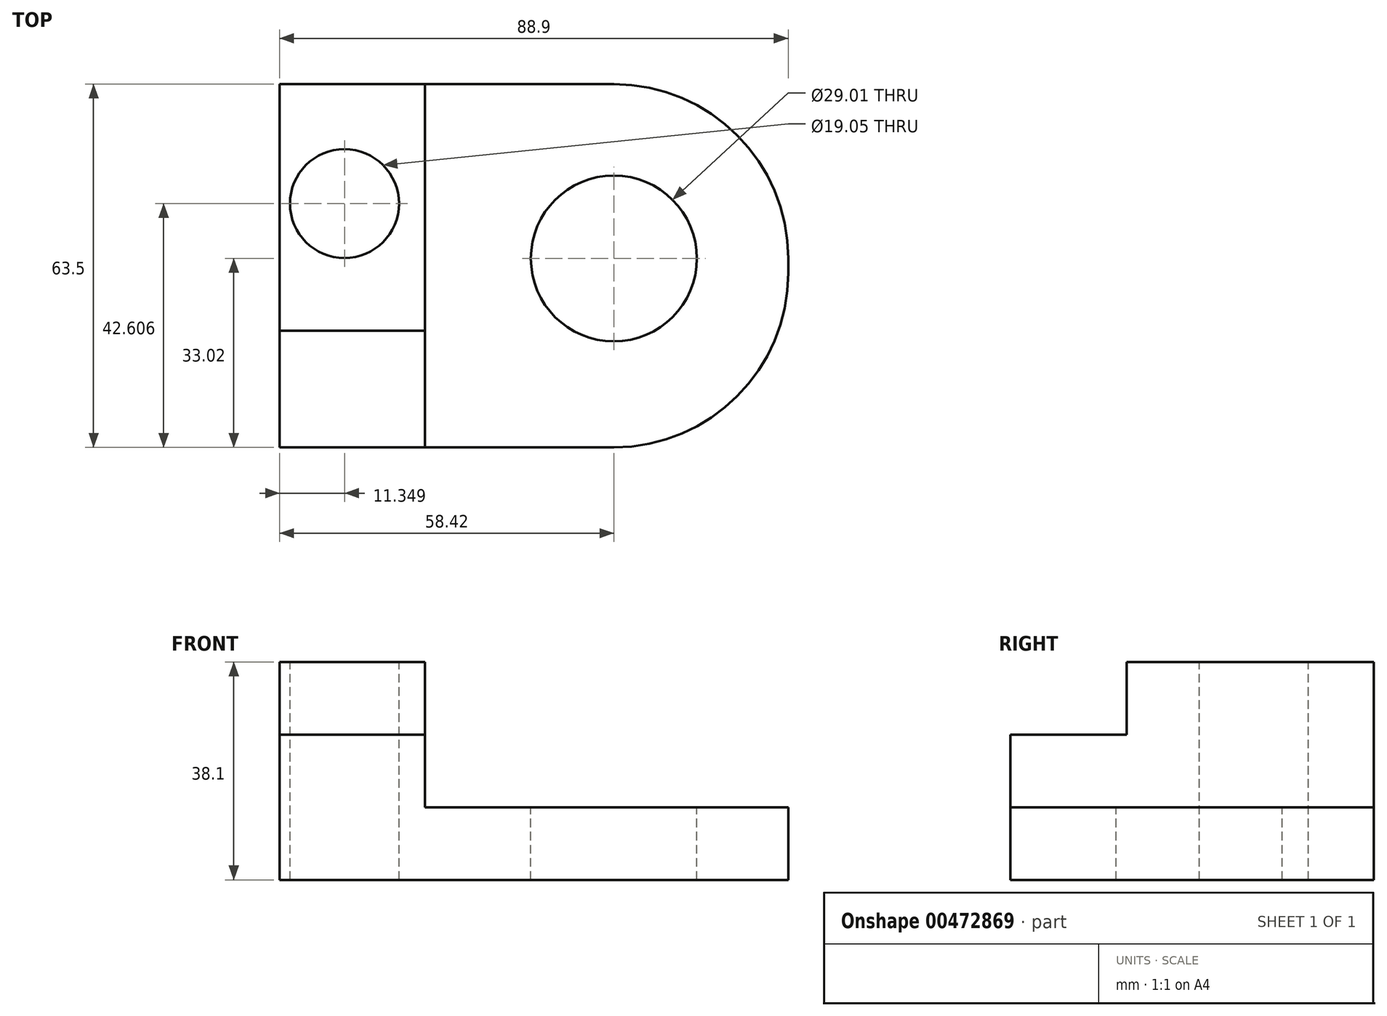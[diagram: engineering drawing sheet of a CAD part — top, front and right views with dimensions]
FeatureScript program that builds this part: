
annotation { "Feature Type Name" : "Feature", "Feature Type Description" : "" }
export const myFeature = defineFeature(function(context is Context, id is Id, definition is map)
    precondition{}
    {
        {
            var Q0;
            Q0=qCreatedBy(makeId("Top.planeOp"),FACE);
            var sketch = newSketch(context, id + "F0", { "sketchPlane" : qUnion([Q0])});
            skLineSegment(sketch, "E0.bottom", {"start": v(13.97, 31.75) * mm, "end": v(-44.45, 31.75) * mm});
            skLineSegment(sketch, "E0.top", {"start": v(13.97, -31.75) * mm, "end": v(-44.45, -31.75) * mm});
            skLineSegment(sketch, "E0.left", {"start": v(44.45, 1.27) * mm, "end": v(44.45, -1.27) * mm});
            skLineSegment(sketch, "E0.right", {"start": v(-44.45, 31.75) * mm, "end": v(-44.45, -31.75) * mm});
            skPoint(sketch, "E0.middle", {"position": v(0, 0) * mm});
            skPoint(sketch, "E1.visualSharp", {"position": v(44.45, 31.75) * mm});
            skArc(sketch, "E1.filletArc", {"start": v(44.45, 1.27) * mm, "mid": v(35.52, 22.82) * mm, "end": v(13.97, 31.75) * mm});
            skPoint(sketch, "E2.visualSharp", {"position": v(44.45, -31.75) * mm});
            skArc(sketch, "E2.filletArc", {"start": v(13.97, -31.75) * mm, "mid": v(35.52, -22.82) * mm, "end": v(44.45, -1.27) * mm});
            skSolve(sketch);
        }
        {
            var Q0;
            Q0=makeQuery(id+"F0.imprint","IMPRINT",FACE,{"disambiguationData":[TD([[makeQuery(id+"F0.imprint","IMPRINT",EDGE,{"derivedFrom":sQuery(id+"F0.wireOp",EDGE,"E0.bottom")}),1.0]])]});
            extrude(context, id + "F1", {"entities" : qUnion([Q0]), "depth" : 12.7 * mm});
        }
        {
            var Q0;
            Q0=makeQuery(id+"F1.opExtrude","CAP_FACE",FACE,{"disambiguationData":[OSD([sQuery(id+"F0.wireOp",EDGE,"E0.bottom"),sQuery(id+"F0.wireOp",EDGE,"E0.top"),sQuery(id+"F0.wireOp",EDGE,"E0.left"),sQuery(id+"F0.wireOp",EDGE,"E0.right"),sQuery(id+"F0.wireOp",EDGE,"E1.filletArc"),sQuery(id+"F0.wireOp",EDGE,"E2.filletArc")])],"isStart":false});
            var sketch = newSketch(context, id + "F2", { "sketchPlane" : qUnion([Q0])});
            skLineSegment(sketch, "E3.bottom", {"start": v(-44.45, -31.75) * mm, "end": v(-19.05, -31.75) * mm});
            skLineSegment(sketch, "E3.top", {"start": v(-44.45, 31.75) * mm, "end": v(-19.05, 31.75) * mm});
            skLineSegment(sketch, "E3.left", {"start": v(-44.45, -31.75) * mm, "end": v(-44.45, 31.75) * mm});
            skLineSegment(sketch, "E3.right", {"start": v(-19.05, -31.75) * mm, "end": v(-19.05, 31.75) * mm});
            skSolve(sketch);
        }
        {
            var Q0;
            Q0=makeQuery(id+"F2.imprint","IMPRINT",FACE,{"disambiguationData":[TD([[makeQuery(id+"F2.imprint","IMPRINT",EDGE,{"derivedFrom":sQuery(id+"F2.wireOp",EDGE,"E3.bottom")}),-1.0]])]});
            extrude(context, id + "F3", {"entities" : qUnion([Q0]), "operationType" : NewBodyOperationType.ADD, "depth" : 12.7 * mm});
        }
        {
            var Q0;
            Q0=makeQuery(id+"F3.opExtrude","CAP_FACE",FACE,{"disambiguationData":[OSD([sQuery(id+"F2.wireOp",EDGE,"E3.bottom"),sQuery(id+"F2.wireOp",EDGE,"E3.top"),sQuery(id+"F2.wireOp",EDGE,"E3.left"),sQuery(id+"F2.wireOp",EDGE,"E3.right")])],"isStart":false});
            var sketch = newSketch(context, id + "F4", { "sketchPlane" : qUnion([Q0])});
            skLineSegment(sketch, "E4.bottom", {"start": v(-44.45, 31.75) * mm, "end": v(-19.05, 31.75) * mm});
            skLineSegment(sketch, "E4.top", {"start": v(-44.45, -11.39) * mm, "end": v(-19.05, -11.39) * mm});
            skLineSegment(sketch, "E4.left", {"start": v(-44.45, 31.75) * mm, "end": v(-44.45, -11.39) * mm});
            skLineSegment(sketch, "E4.right", {"start": v(-19.05, 31.75) * mm, "end": v(-19.05, -11.39) * mm});
            skSolve(sketch);
        }
        {
            var Q0;
            Q0=makeQuery(id+"F4.imprint","IMPRINT",FACE,{"disambiguationData":[TD([[makeQuery(id+"F4.imprint","IMPRINT",EDGE,{"derivedFrom":sQuery(id+"F4.wireOp",EDGE,"E4.bottom")}),1.0]])]});
            extrude(context, id + "F5", {"entities" : qUnion([Q0]), "operationType" : NewBodyOperationType.ADD, "depth" : 12.7 * mm});
        }
        {
            var Q0;
            Q0=makeQuery(id+"F1.opExtrude","CAP_FACE",FACE,{"disambiguationData":[OSD([sQuery(id+"F0.wireOp",EDGE,"E0.bottom"),sQuery(id+"F0.wireOp",EDGE,"E0.top"),sQuery(id+"F0.wireOp",EDGE,"E0.left"),sQuery(id+"F0.wireOp",EDGE,"E0.right"),sQuery(id+"F0.wireOp",EDGE,"E1.filletArc"),sQuery(id+"F0.wireOp",EDGE,"E2.filletArc")])],"isStart":false});
            var sketch = newSketch(context, id + "F6", { "sketchPlane" : qUnion([Q0])});
            skCircle(sketch, "E5", {"center": v(13.97, 1.27) * mm, "radius": 14.5 * mm});
            skSolve(sketch);
        }
        {
            var Q0;
            Q0=makeQuery(id+"F6.imprint","IMPRINT",FACE,{"disambiguationData":[TD([[makeQuery(id+"F6.imprint","IMPRINT",EDGE,{"derivedFrom":sQuery(id+"F6.wireOp",EDGE,"E5")}),1.0]])]});
            extrude(context, id + "F7", {"entities" : qUnion([Q0]), "operationType" : NewBodyOperationType.REMOVE, "endBound" : BoundingType.THROUGH_ALL, "oppositeDirection" : true, "depth" : 25.4 * mm});
        }
        {
            var Q0;
            Q0=makeQuery(id+"F5.opExtrude","CAP_FACE",FACE,{"disambiguationData":[OSD([sQuery(id+"F4.wireOp",EDGE,"E4.bottom"),sQuery(id+"F4.wireOp",EDGE,"E4.top"),sQuery(id+"F4.wireOp",EDGE,"E4.left"),sQuery(id+"F4.wireOp",EDGE,"E4.right")])],"isStart":false});
            var sketch = newSketch(context, id + "F8", { "sketchPlane" : qUnion([Q0])});
            skPoint(sketch, "E6", {"position": v(-33.1, 10.86) * mm});
            skSolve(sketch);
        }
        {
            var Q0;
            Q0=sQuery(id+"F8.wireOp",VERTEX,"E6");
            var Q1;
            Q1=makeQuery(id+"F1.opExtrude","SWEPT_BODY",BODY,{"disambiguationData":[OSD([sQuery(id+"F0.wireOp",EDGE,"E0.bottom"),sQuery(id+"F0.wireOp",EDGE,"E0.top"),sQuery(id+"F0.wireOp",EDGE,"E0.left"),sQuery(id+"F0.wireOp",EDGE,"E0.right"),sQuery(id+"F0.wireOp",EDGE,"E1.filletArc"),sQuery(id+"F0.wireOp",EDGE,"E2.filletArc")])]});
            hole(context, id + "F9", {"style" : HoleStyle.SIMPLE, "endStyle" : HoleEndStyle.THROUGH, "holeDiameter" : 19.05 * mm, "isTappedThrough" : true, "tappedDepth" : 12.7 * mm, "tapClearance" : 3, "locations" : qUnion([Q0]), "scope" : qUnion([Q1])});
        }
    });
